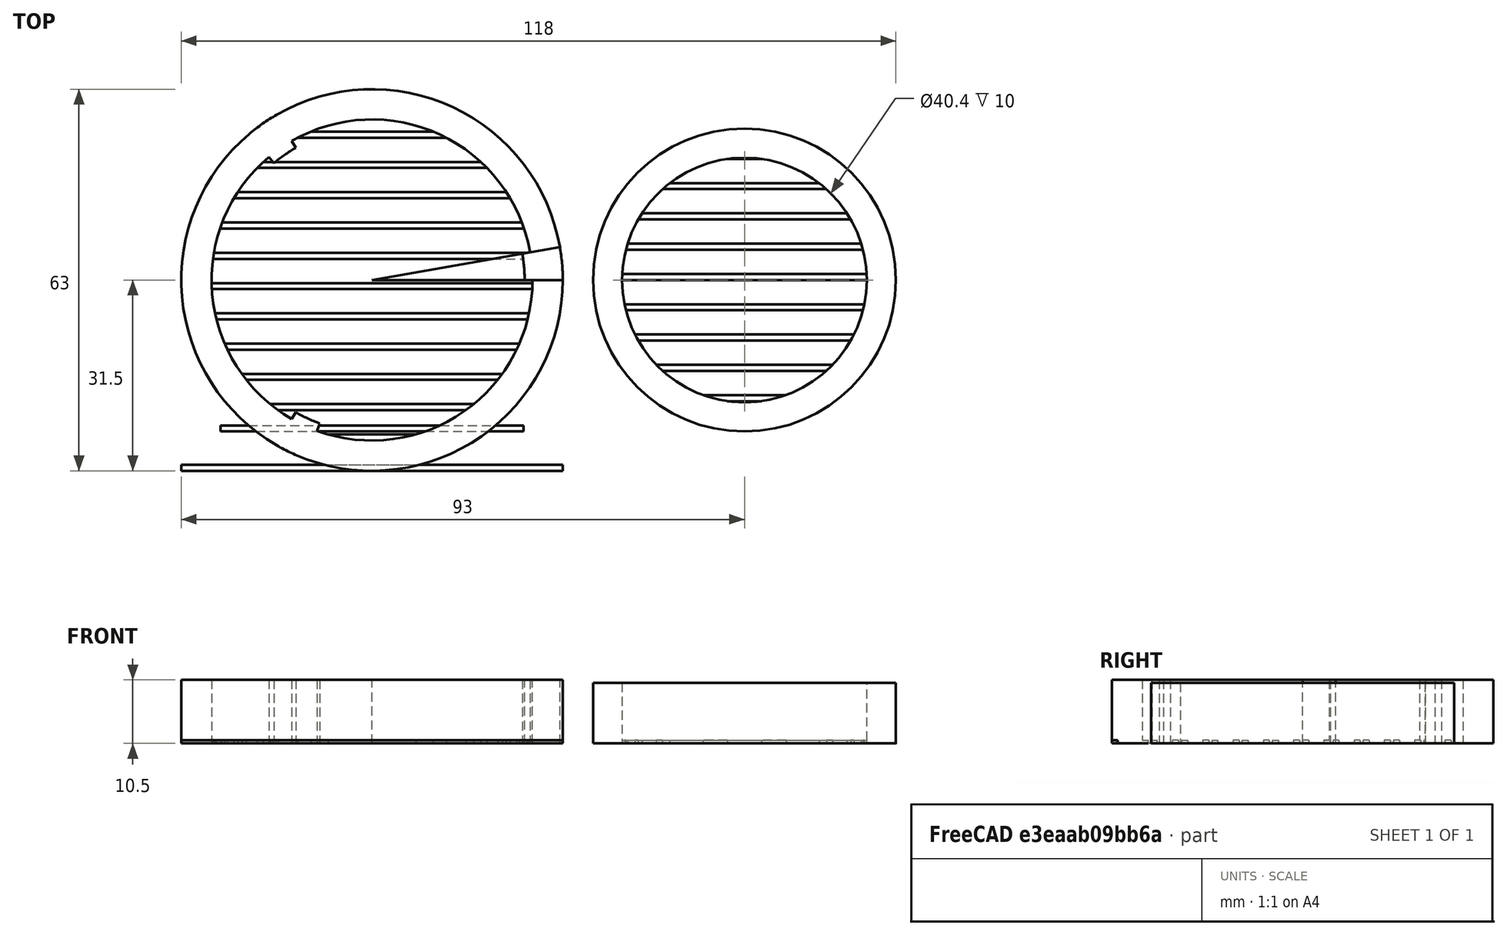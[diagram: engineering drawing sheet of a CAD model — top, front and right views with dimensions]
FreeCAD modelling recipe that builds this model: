
FCSTD DOCUMENT  (FreeCAD 1.0R39285 (Git))
Label: doubletopmarkingpot
License: All rights reserved
LicenseURL: https://en.wikipedia.org/wiki/All_rights_reserved
objects: Part::Cylinder×6, Part::FeaturePython×3, Part::Cut×3, Part::Box×2, Part::MultiCommon×2, Part::MultiFuse×2, Spreadsheet::Sheet×1, App::Part×1
note: 15 computed .brp shape members not serialized (recipe doc carries the construction recipe); baked Part::Feature solids carry a one-line shape summary decoded from their .brp

FEATURE [Spreadsheet::Sheet] Spreadsheet
  cells = A1='Tube Tolerance; B1(tube_tolerance)=0.2; C1='mm; D1='How much extra space does the tube need?; A2='Tube Outer Diameter; B2(tube_outer_diameter)=40; C2='mm; D2='Diameter of plastic marking pot tube; A3='First Lid Outer Diameter; B3(first_lid_outer_diameter)=50; C3='mm; D3='Outer diameter of the first lid (that goes on the pot); A4='First Lid Height; B4(first_lid_height)=10; C4='mm; D4='Height of the first lid, this minus the line depth overlaps the tube; A5='First Lid Line Spacing; B5(first_lid_line_spacing)=5; C5='mm; D5='Spacing of lines in first lid. Note: The gaps have width:; E5==first_lid_line_spacing - first_lid_line_widths; F5='mm; A6='First Lid Line Widths; B6(first_lid_line_widths)=1; C6='mm; D6='How wide the actual grid's lines are; A7='First Lid Line Depth; B7(first_lid_line_depth)=0.5; C7='mm; D7='How deep the grid lines are (0.5mm might be ok?); A8='Second Lid Outer Diameter; B8(second_lid_outer_diameter)=63; C8='mm; D8='Outer diameter of the second lid (that goes on the first); A9='Second Lid Height; B9(second_lid_height)=10.5; C9='mm; D9='The height of the second lid.'Recommend:; E9==first_lid_height + first_lid_line_depth; F9='mm; A10='Second Lid Tolerance; B10(second_lid_tolerance)=0.2; C10='mm; D10='How much extra space is needed between the two lids; A11='Second Lid Line Spacing; B11(second_lid_line_spacing)=5; C11='mm; D11='Spacing of lines in second lid. Note: The gaps have width:; E11==second_lid_line_spacing - second_lid_line_widths; F11='mm; A12='Second Lid Line Widths; B12(second_lid_line_widths)=1; C12='mm; D12='How wide the actual grid's lines are; A13='Second Lid Line Depth; B13(second_lid_line_depth)=0.5; C13='mm; D13='How deep the grid lines are (0.5mm might be ok?); A14='Second Lid Inner Diameter; B14(second_lid_inner_diameter)=53; C14='mm; D14='This lid's inner diameter is wider than the other lid (rather than having it snug the whole circumference); A15='Second Lid Grip Size (degrees); B15(second_lid_grip_size)=10; C15='degrees; D15='How big each grip should be. This equates to each grip having contact length of; E15==2 * 3.14159 * first_lid_outer_diameter / 2 * second_lid_grip_size / 360; F15='mm; A16='Second Lid Grip Count; B16(second_lid_grip_count)=3; C16='count; D16='The number of grips.; A17='Calculated from the above parameter (do not change):; A18='First Lid Line Count; B18(first_lid_line_count)==ceil(first_lid_outer_diameter / first_lid_line_spacing) + 1; A19='Second Lid Line Count; B19(second_lid_line_count)==ceil(second_lid_outer_diameter / second_lid_line_spacing) + 1
FEATURE [Part::Cylinder] Cylinder  label="TubeCutCylinder"
  Angle = 360
  AttacherType = Attacher::AttachEngine3D
  FirstAngle = 0
  Height = 50
  Radius = 20.2
  SecondAngle = 0
  expr: Radius = <<Spreadsheet>>.tube_outer_diameter / 2 + <<Spreadsheet>>.tube_tolerance
FEATURE [Part::Cylinder] Cylinder001  label="FirstCylinder"
  Angle = 360
  AttacherType = Attacher::AttachEngine3D
  FirstAngle = 0
  Height = 10
  Radius = 25
  SecondAngle = 0
  expr: Height = <<Spreadsheet>>.first_lid_height
  expr: Radius = <<Spreadsheet>>.first_lid_outer_diameter / 2
FEATURE [Part::Box] Box  label="Cube"
  AttacherType = Attacher::AttachEngine3D
  Height = 0.5
  Length = 50
  Placement = pos=(-25,-25,0) rot=(0,0,1;0rad)
  Width = 1
  expr: .Placement.Base.x = -<<Spreadsheet>>.first_lid_outer_diameter / 2
  expr: .Placement.Base.y = -<<Spreadsheet>>.first_lid_outer_diameter / 2
  expr: Height = <<Spreadsheet>>.first_lid_line_depth
  expr: Length = <<Spreadsheet>>.first_lid_outer_diameter
  expr: Width = <<Spreadsheet>>.first_lid_line_widths
FEATURE [Part::FeaturePython] Array  label="FirstLidGridFull"  # Draft array (typed FeaturePython)
  AlwaysSyncPlacement = false
  Angle = 360
  ArrayType = 0
  Axis = (0,0,1)
  Base = -> Box
  Center = (0,0,0)
  Count = 11
  ExpandArray = false
  Fuse = false
  IntervalAxis = (0,0,0)
  IntervalX = (0,0,0)
  IntervalY = (0,5,0)
  IntervalZ = (0,0,100)
  NumberCircles = 3
  NumberPolar = 5
  NumberX = 1
  NumberY = 11
  NumberZ = 1
  PlacementList = 11 placements: arithmetic series from (-25,-25,0) step (0,5,0) to (-25,25,0)
  RadialDistance = 50
  ScaleList = (11) [(1,1,1),(1,1,1),(1,1,1),(1,1,1),(1,1,1),(1,1,1),(1,1,1),(1,1,1),(1,1,1),(1,1,1),(1,1,1)]
  Symmetry = 1
  TangentialDistance = 25
  expr: .IntervalY.y = <<Spreadsheet>>.first_lid_line_spacing
  expr: NumberY = <<Spreadsheet>>.first_lid_line_count
FEATURE [Part::MultiCommon] Common  label="FirstLidGrid"
  Shapes = -> [Cylinder001,Array]
FEATURE [Part::Cut] Cut  label="FirstLidEdge"
  Base = -> Cylinder001
  Tool = -> Cylinder
FEATURE [Part::Cylinder] Cylinder002  label="SecondCylinder"
  Angle = 360
  AttacherType = Attacher::AttachEngine3D
  FirstAngle = 0
  Height = 10.5
  Radius = 31.5
  SecondAngle = 0
  expr: Height = <<Spreadsheet>>.second_lid_height
  expr: Radius = <<Spreadsheet>>.second_lid_outer_diameter / 2
FEATURE [Part::Cylinder] Cylinder003  label="SecondCylinderGripCut"
  Angle = 360
  AttacherType = Attacher::AttachEngine3D
  FirstAngle = 0
  Height = 10.5
  Radius = 25.2
  SecondAngle = 0
  expr: Height = <<Spreadsheet>>.second_lid_height
  expr: Radius = <<Spreadsheet>>.first_lid_outer_diameter / 2 + <<Spreadsheet>>.second_lid_tolerance
FEATURE [Part::Cylinder] Cylinder004  label="SecondCylinderCut"
  Angle = 360
  AttacherType = Attacher::AttachEngine3D
  FirstAngle = 0
  Height = 10.5
  Radius = 26.5
  SecondAngle = 0
  expr: Height = <<Spreadsheet>>.second_lid_height
  expr: Radius = <<Spreadsheet>>.second_lid_inner_diameter / 2
FEATURE [Part::Cut] Cut001  label="SecondLid"
  Base = -> Cylinder002
  Tool = -> Cylinder004
FEATURE [Part::Cylinder] Cylinder005  label="Grip"
  Angle = 10
  AttacherType = Attacher::AttachEngine3D
  FirstAngle = 0
  Height = 10.5
  Radius = 31.5
  SecondAngle = 0
  expr: Angle = <<Spreadsheet>>.second_lid_grip_size
  expr: Height = <<Spreadsheet>>.second_lid_height
  expr: Radius = <<Spreadsheet>>.second_lid_outer_diameter / 2
FEATURE [Part::FeaturePython] Array001  label="GripArray"  # Draft array (typed FeaturePython)
  AlwaysSyncPlacement = false
  Angle = 360
  ArrayType = 1
  Axis = (0,0,1)
  Base = -> Cylinder005
  Center = (0,0,0)
  Count = 3
  ExpandArray = false
  Fuse = false
  IntervalAxis = (0,0,0)
  IntervalX = (50,0,0)
  IntervalY = (0,50,0)
  IntervalZ = (0,0,50)
  NumberCircles = 3
  NumberPolar = 3
  NumberX = 2
  NumberY = 2
  NumberZ = 1
  PlacementList = 3 placements: [(0,0,0),(0,0,0),(0,0,0)]
  RadialDistance = 50
  ScaleList = (3) [(1,1,1),(1,1,1),(1,1,1)]
  Symmetry = 1
  TangentialDistance = 25
  expr: NumberPolar = <<Spreadsheet>>.second_lid_grip_count
FEATURE [Part::Cut] Cut002  label="SecondLidGrip"
  Base = -> Array001
  Tool = -> Cylinder003
FEATURE [Part::MultiFuse] Fusion  label="First Lid"
  Placement = pos=(61.5,0,0) rot=(0,0,1;0rad)
  Shapes = -> [Cut,Common]
  expr: .Placement.Base.x = <<Spreadsheet>>.second_lid_outer_diameter / 2 + <<Spreadsheet>>.first_lid_outer_diameter / 2 + 5
FEATURE [Part::Box] Box001  label="Cube001"
  AttacherType = Attacher::AttachEngine3D
  Height = 0.5
  Length = 63
  Placement = pos=(-31.5,-31.5,0) rot=(0,0,1;0rad)
  Width = 1
  expr: .Placement.Base.x = -<<Spreadsheet>>.second_lid_outer_diameter / 2
  expr: .Placement.Base.y = -<<Spreadsheet>>.second_lid_outer_diameter / 2
  expr: Height = <<Spreadsheet>>.second_lid_line_depth
  expr: Length = <<Spreadsheet>>.second_lid_outer_diameter
  expr: Width = <<Spreadsheet>>.second_lid_line_widths
FEATURE [Part::FeaturePython] Array002  # Draft array (typed FeaturePython)
  AlwaysSyncPlacement = false
  Angle = 360
  ArrayType = 0
  Axis = (0,0,1)
  Base = -> Box001
  Center = (0,0,0)
  Count = 14
  ExpandArray = false
  Fuse = false
  IntervalAxis = (0,0,0)
  IntervalX = (100,0,0)
  IntervalY = (0,5,0)
  IntervalZ = (0,0,100)
  NumberCircles = 3
  NumberPolar = 5
  NumberX = 1
  NumberY = 14
  NumberZ = 1
  PlacementList = 14 placements: arithmetic series from (-31.5,-31.5,0) step (0,5,0) to (-31.5,33.5,0)
  RadialDistance = 50
  ScaleList = (14) [(1,1,1),(1,1,1),(1,1,1),(1,1,1),(1,1,1),(1,1,1),(1,1,1),(1,1,1),(1,1,1),(1,1,1),(1,1,1),(1,1,1),(1,1,1),(1,1,1)]
  Symmetry = 1
  TangentialDistance = 25
  expr: .IntervalY.y = <<Spreadsheet>>.second_lid_line_spacing
  expr: NumberY = <<Spreadsheet>>.second_lid_line_count
FEATURE [Part::MultiCommon] Common001  label="SecondLidGrid"
  Shapes = -> [Array002,Cylinder002]
FEATURE [Part::MultiFuse] Fusion001  label="Second Lid"
  Shapes = -> [Cut002,Cut001,Common001]
FEATURE [App::Part] Part
  Group = -> [Box,Cylinder005,Array,Common,Cylinder001,Cylinder,Cut,Fusion,Box001,Cylinder002,Cylinder003,Cylinder004,Cut001,Array001,Cut002,Common001,Array002,Fusion001]
  Origin = -> Origin
